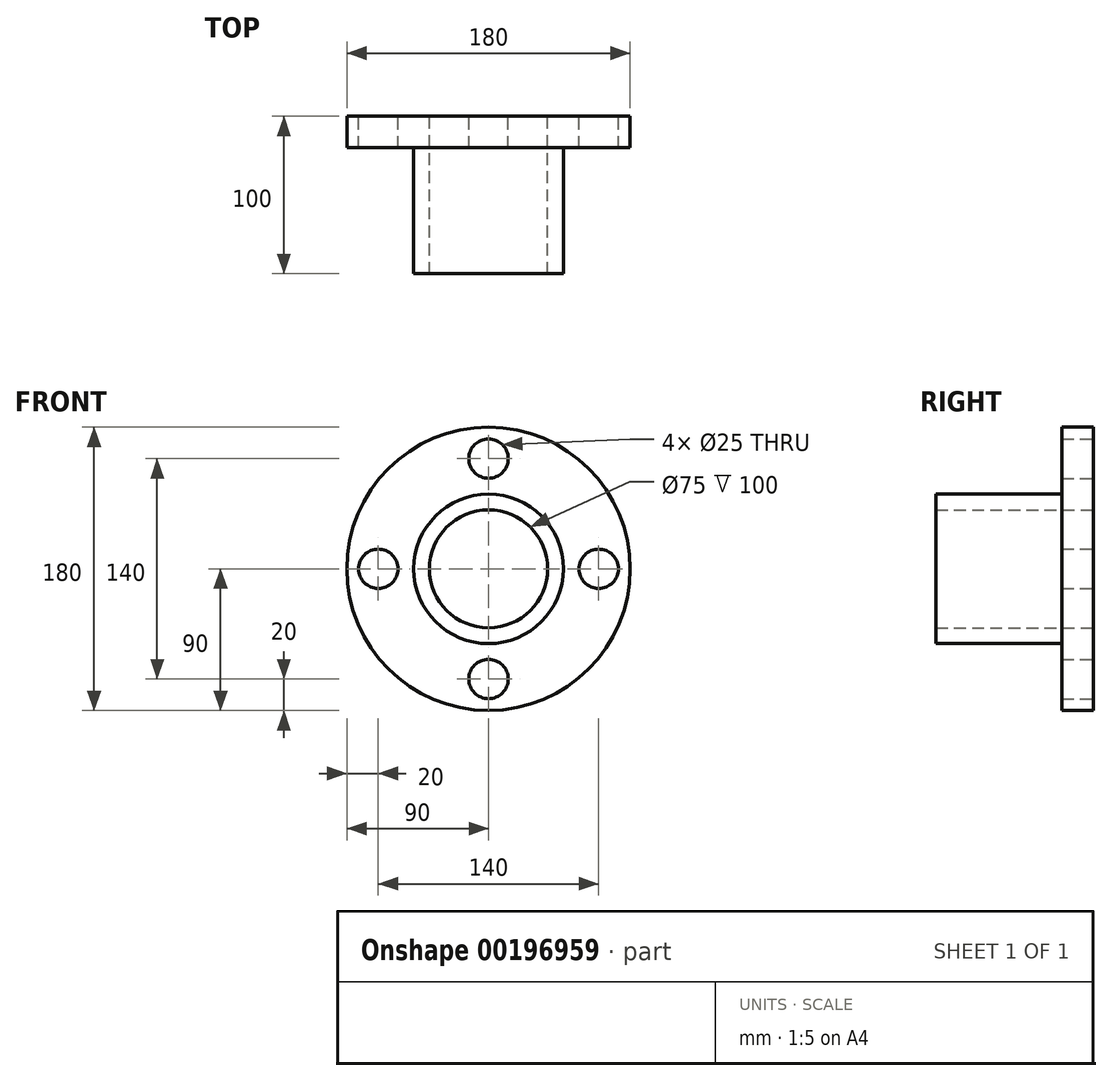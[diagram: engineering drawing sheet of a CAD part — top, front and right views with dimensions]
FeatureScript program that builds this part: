
annotation { "Feature Type Name" : "Feature", "Feature Type Description" : "" }
export const myFeature = defineFeature(function(context is Context, id is Id, definition is map)
    precondition{}
    {
        {
            var Q0;
            Q0=qCreatedBy(makeId("Front.planeOp"),FACE);
            var sketch = newSketch(context, id + "F0", { "sketchPlane" : qUnion([Q0])});
            skCircle(sketch, "E0", {"center": v(0, 0) * mm, "radius": 90 * mm});
            skCircle(sketch, "E1", {"center": v(0, 70) * mm, "radius": 12.5 * mm});
            skCircle(sketch, "E2", {"center": v(0, -70) * mm, "radius": 12.5 * mm});
            skCircle(sketch, "E3", {"center": v(-70, 0) * mm, "radius": 12.5 * mm});
            skCircle(sketch, "E4", {"center": v(70, 0) * mm, "radius": 12.5 * mm});
            skCircle(sketch, "E5", {"center": v(0, 0) * mm, "radius": 70 * mm, "construction": true});
            skCircle(sketch, "E6", {"center": v(0, 0) * mm, "radius": 37.5 * mm});
            skSolve(sketch);
        }
        {
            var Q0;
            Q0=makeQuery(id+"F0.imprint","IMPRINT",FACE,{"disambiguationData":[TD([[makeQuery(id+"F0.imprint","IMPRINT",EDGE,{"derivedFrom":sQuery(id+"F0.wireOp",EDGE,"E0")}),1.0]])]});
            extrude(context, id + "F1", {"entities" : qUnion([Q0]), "depth" : 20 * mm});
        }
        {
            var Q0;
            Q0=makeQuery(id+"F1.opExtrude","CAP_FACE",FACE,{"disambiguationData":[OSD([sQuery(id+"F0.wireOp",EDGE,"E0"),sQuery(id+"F0.wireOp",EDGE,"E1"),sQuery(id+"F0.wireOp",EDGE,"E2"),sQuery(id+"F0.wireOp",EDGE,"E3"),sQuery(id+"F0.wireOp",EDGE,"E4"),sQuery(id+"F0.wireOp",EDGE,"E6")])],"isStart":false});
            var sketch = newSketch(context, id + "F2", { "sketchPlane" : qUnion([Q0])});
            skCircle(sketch, "E7.0", {"center": v(0, 0) * mm, "radius": 37.5 * mm});
            skCircle(sketch, "E8", {"center": v(0, 0) * mm, "radius": 47.5 * mm});
            skSolve(sketch);
        }
        {
            var Q0;
            Q0 = qSketchRegion(id + "F2", true);
            extrude(context, id + "F3", {"entities" : qUnion([Q0]), "operationType" : NewBodyOperationType.ADD, "depth" : 80 * mm});
        }
    });
